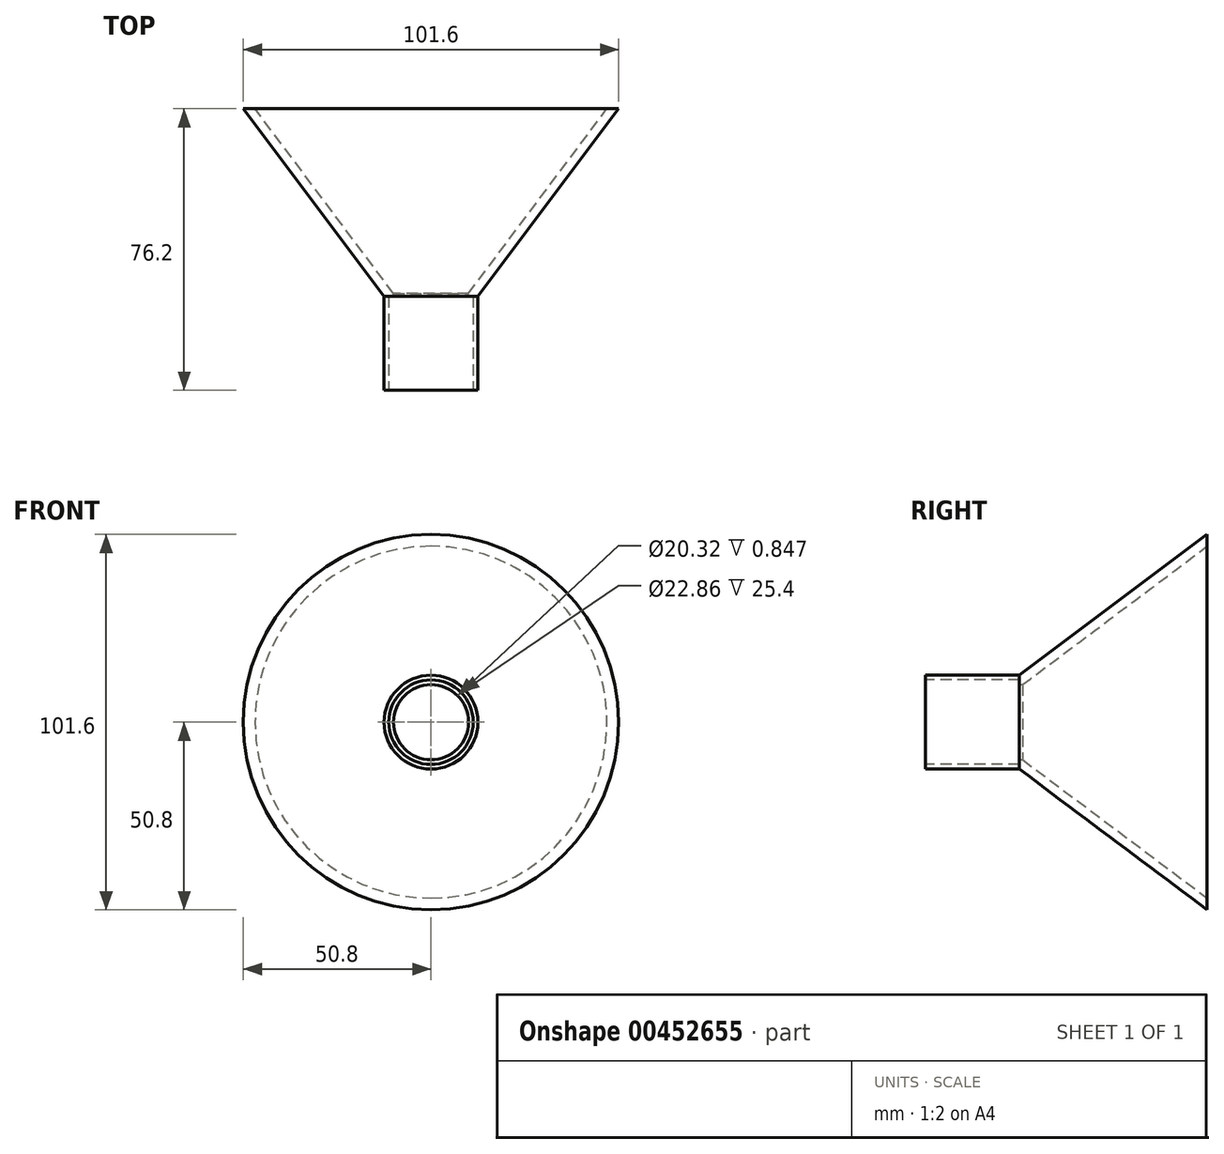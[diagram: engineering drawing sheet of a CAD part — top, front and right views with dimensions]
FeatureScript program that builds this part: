
annotation { "Feature Type Name" : "Feature", "Feature Type Description" : "" }
export const myFeature = defineFeature(function(context is Context, id is Id, definition is map)
    precondition{}
    {
        {
            var Q0;
            Q0=qCreatedBy(makeId("Front.planeOp"),FACE);
            var sketch = newSketch(context, id + "F0", { "sketchPlane" : qUnion([Q0])});
            skCircle(sketch, "E0", {"center": v(0, 0) * mm, "radius": 50.8 * mm});
            skSolve(sketch);
        }
        {
            var Q0;
            Q0=makeQuery(id+"F0.imprint","IMPRINT",FACE,{"disambiguationData":[TD([[makeQuery(id+"F0.imprint","IMPRINT",EDGE,{"derivedFrom":sQuery(id+"F0.wireOp",EDGE,"E0")}),1.0]])]});
            cPlane(context, id + "F1", {"entities" : qUnion([Q0]), "cplaneType" : CPlaneType.OFFSET, "offset" : 50.8 * mm, "width" : 152.4 * mm, "height" : 152.4 * mm});
        }
        {
            var Q0;
            Q0=qCreatedBy(id+"F1.planeOp",FACE);
            var sketch = newSketch(context, id + "F2", { "sketchPlane" : qUnion([Q0])});
            skCircle(sketch, "E1", {"center": v(0, 0) * mm, "radius": 12.7 * mm});
            skSolve(sketch);
        }
        {
            var Q0;
            Q0 = qSketchRegion(id + "F2", true);
            extrude(context, id + "F3", {"entities" : qUnion([Q0]), "depth" : 25.4 * mm});
        }
        {
            var Q1;
            Q1=makeQuery(id+"F3.opExtrude","CAP_FACE",FACE,{"disambiguationData":[OSD([sQuery(id+"F2.wireOp",EDGE,"E1")])],"isStart":true});
            var Q2;
            Q2=makeQuery(id+"F0.imprint","IMPRINT",FACE,{"disambiguationData":[TD([[makeQuery(id+"F0.imprint","IMPRINT",EDGE,{"derivedFrom":sQuery(id+"F0.wireOp",EDGE,"E0")}),1.0]])]});
            loft(context, id + "F4", {"operationType" : NewBodyOperationType.ADD, "sheetProfilesArray" : [{ "sheetProfileEntities" : qUnion([Q1]) }, { "sheetProfileEntities" : qUnion([Q2]) }]});
        }
        {
            var Q0;
            Q0=makeQuery(id+"F4.opLoft","CAP_FACE",FACE,{"disambiguationData":[OSD([makeQuery(id+"F0.imprint","IMPRINT",FACE,{"disambiguationData":[TD([[makeQuery(id+"F0.imprint","IMPRINT",EDGE,{"derivedFrom":sQuery(id+"F0.wireOp",EDGE,"E0")}),1.0]])]})])],"isStart":true});
            shell(context, id + "F5", {"entities" : qUnion([Q0]), "thickness" : 2.54 * mm});
        }
        {
            var Q0;
            Q0=makeQuery(id+"F3.opExtrude","CAP_FACE",FACE,{"disambiguationData":[OSD([sQuery(id+"F2.wireOp",EDGE,"E1")])],"isStart":false});
            var sketch = newSketch(context, id + "F6", { "sketchPlane" : qUnion([Q0])});
            skCircle(sketch, "E2", {"center": v(0, 0) * mm, "radius": 11.43 * mm});
            skSolve(sketch);
        }
        {
            var Q0;
            Q0=makeQuery(id+"F6.imprint","IMPRINT",FACE,{"disambiguationData":[TD([[makeQuery(id+"F6.imprint","IMPRINT",EDGE,{"derivedFrom":sQuery(id+"F6.wireOp",EDGE,"E2")}),1.0]])]});
            extrude(context, id + "F7", {"entities" : qUnion([Q0]), "operationType" : NewBodyOperationType.REMOVE, "oppositeDirection" : true, "depth" : 25.4 * mm});
        }
    });
